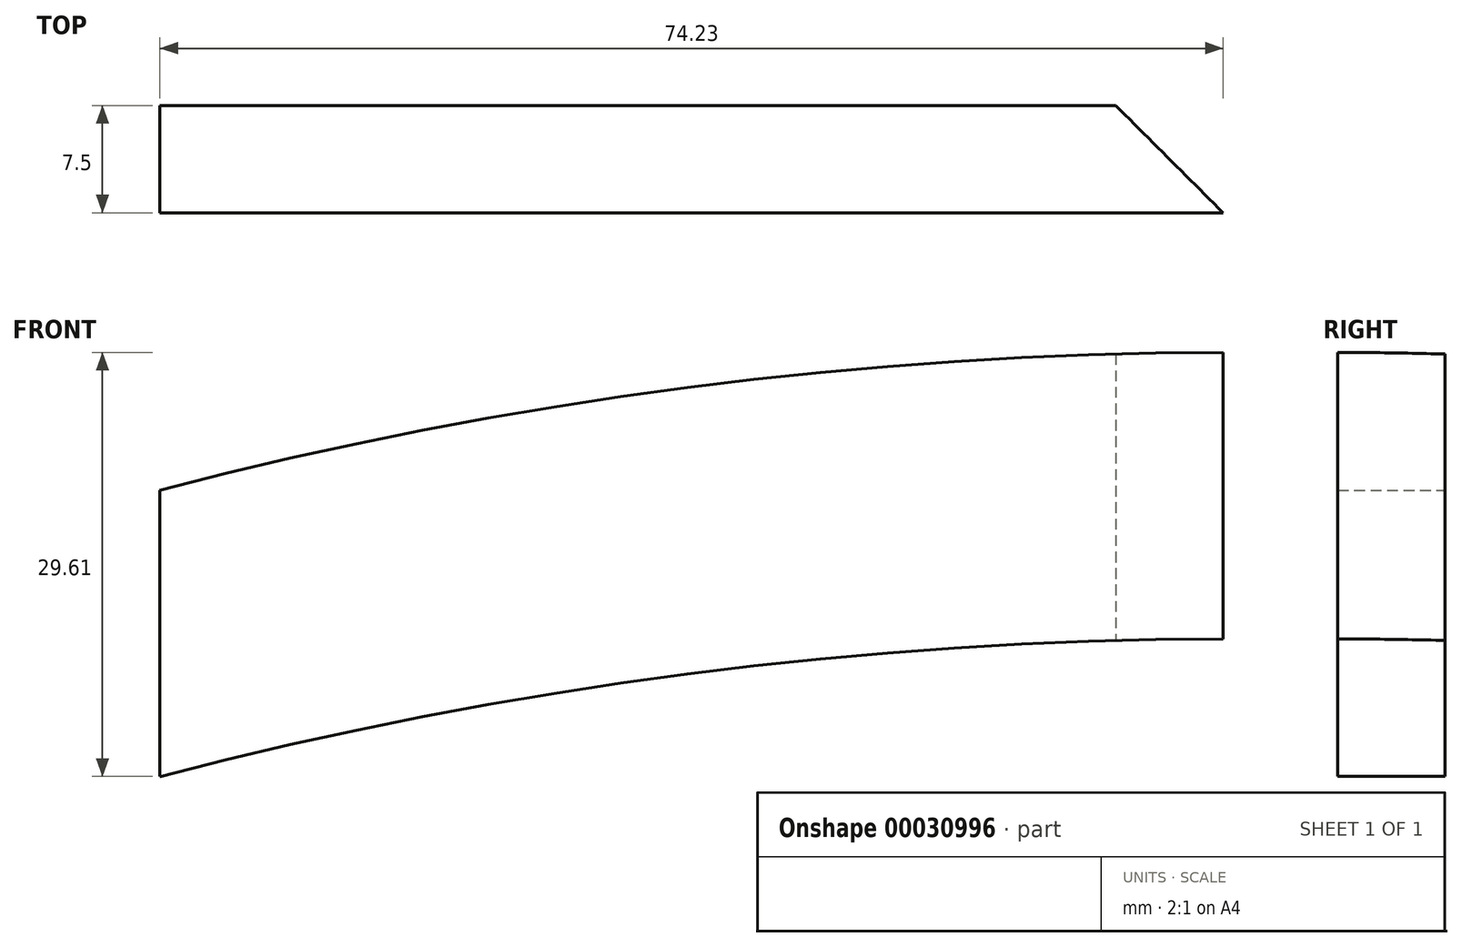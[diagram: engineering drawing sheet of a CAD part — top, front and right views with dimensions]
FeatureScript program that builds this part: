
annotation { "Feature Type Name" : "Feature", "Feature Type Description" : "" }
export const myFeature = defineFeature(function(context is Context, id is Id, definition is map)
    precondition{}
    {
        {
            var Q0;
            Q0=qCreatedBy(makeId("Front.planeOp"),FACE);
            var sketch = newSketch(context, id + "F0", { "sketchPlane" : qUnion([Q0])});
            skLineSegment(sketch, "E0", {"start": v(-74.73, 0) * mm, "end": v(-74.73, 20) * mm});
            skArc(sketch, "E1", {"start": v(0, 29.61) * mm, "mid": v(-37.67, 27.2) * mm, "end": v(-74.73, 20) * mm});
            skArc(sketch, "E2", {"start": v(0, 9.61) * mm, "mid": v(-37.67, 7.2) * mm, "end": v(-74.73, 0) * mm});
            skLineSegment(sketch, "E3", {"start": v(0, 29.61) * mm, "end": v(0, 9.61) * mm});
            skLineSegment(sketch, "E4", {"start": v(-74.73, 0) * mm, "end": v(-83, 17.77) * mm});
            skLineSegment(sketch, "E5", {"start": v(-83, 17.77) * mm, "end": v(-74.73, 20) * mm});
            skSolve(sketch);
        }
        {
            var Q0;
            {var subQ2=sQuery(id+"F0.wireOp",EDGE,"E0");Q0=makeQuery(id+"F0.imprint","IMPRINT",FACE,{"disambiguationData":[TD([[makeQuery(id+"F0.imprint","IMPRINT",EDGE,{"derivedFrom":subQ2}),-1.0]])]});}
            var Q1;
            {var subQ2=sQuery(id+"F0.wireOp",EDGE,"d5a9f697-a3c0-4d75-bb54-b9e9130054d0");Q1=makeQuery(id+"F0.imprint","IMPRINT",FACE,{"disambiguationData":[TD([[makeQuery(id+"F0.imprint","IMPRINT",EDGE,{"derivedFrom":subQ2}),1.0]])]});}
            extrude(context, id + "F1", {"entities" : qUnion([Q0, Q1]), "depth" : 7.5 * mm});
        }
        {
            var Q0;
            Q0=makeQuery(id+"F1.opExtrude","CAP_EDGE",EDGE,{"disambiguationData":[OSD([sQuery(id+"F0.wireOp",EDGE,"E3")])],"isStart":true});
            chamfer(context, id + "F2", {"entities" : qUnion([Q0]), "width" : 8 * mm, "tangentPropagation" : true});
        }
    });
